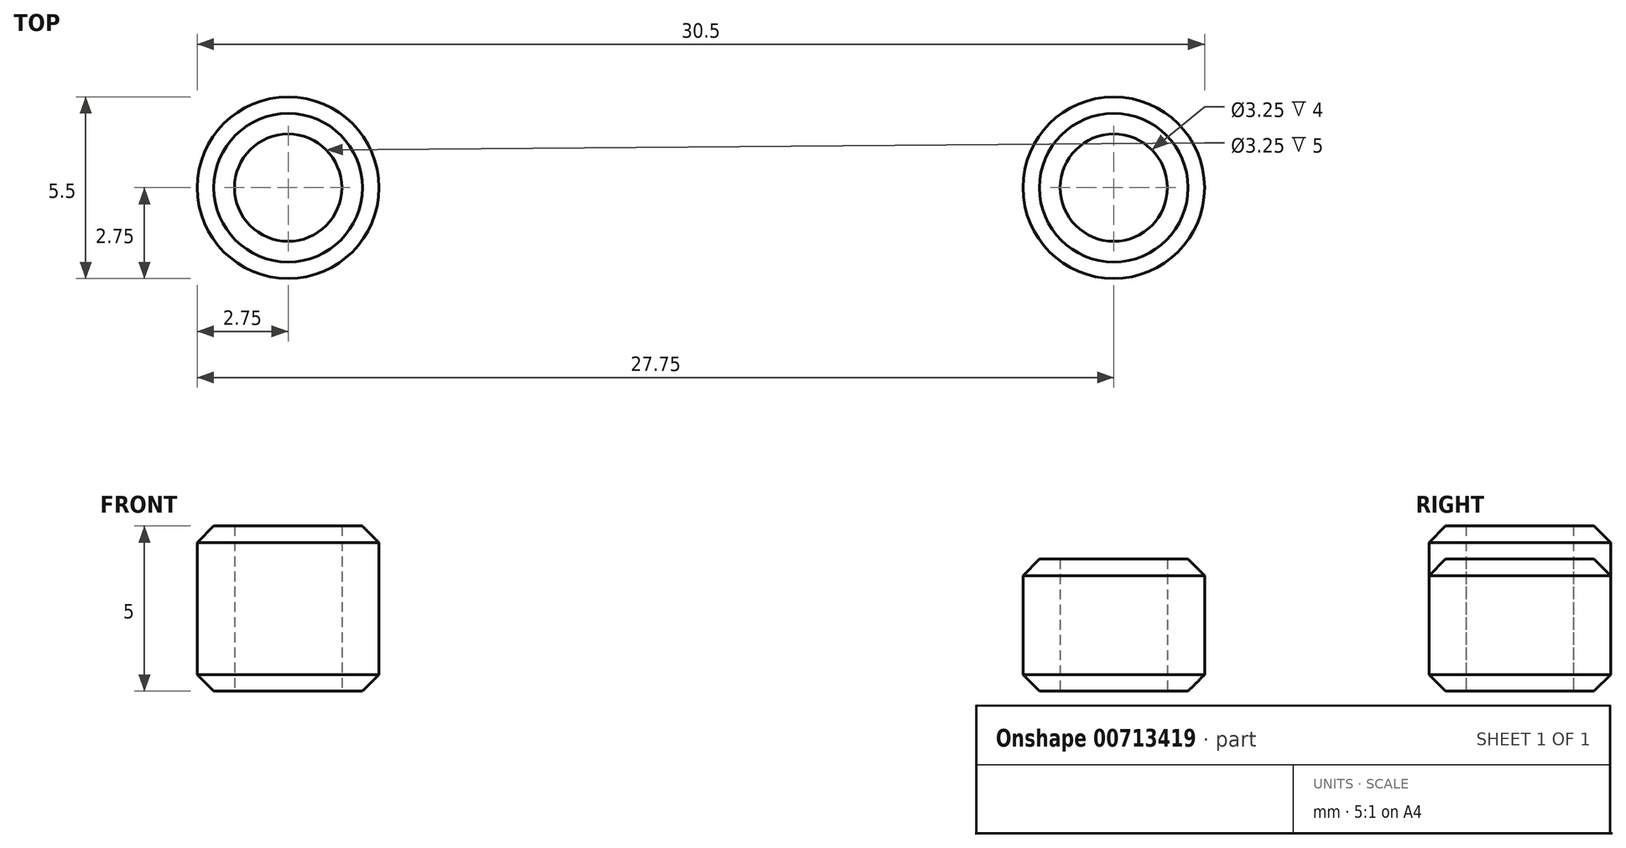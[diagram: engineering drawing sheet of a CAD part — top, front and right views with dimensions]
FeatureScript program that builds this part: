
annotation { "Feature Type Name" : "Feature", "Feature Type Description" : "" }
export const myFeature = defineFeature(function(context is Context, id is Id, definition is map)
    precondition{}
    {
        {
            var Q0;
            Q0=qCreatedBy(makeId("Top.planeOp"),FACE);
            var sketch = newSketch(context, id + "F0", { "sketchPlane" : qUnion([Q0])});
            skCircle(sketch, "E0", {"center": v(0, 0) * mm, "radius": 2.75 * mm});
            skCircle(sketch, "E1", {"center": v(0, 0) * mm, "radius": 1.63 * mm});
            skCircle(sketch, "E2.1.0.0", {"center": v(25, 0) * mm, "radius": 1.63 * mm});
            skCircle(sketch, "E2.1.0.1", {"center": v(25, 0) * mm, "radius": 2.75 * mm});
            skLineSegment(sketch, "E2.direction1", {"start": v(0, 0) * mm, "end": v(25, 0) * mm, "construction": true});
            skSolve(sketch);
        }
        {
            var Q0;
            Q0=makeQuery(id+"F0.imprint","IMPRINT",FACE,{"disambiguationData":[TD([[makeQuery(id+"F0.imprint","IMPRINT",EDGE,{"derivedFrom":sQuery(id+"F0.wireOp",EDGE,"E0")}),1.0]])]});
            extrude(context, id + "F1", {"entities" : qUnion([Q0]), "depth" : 5 * mm, "offsetDistance" : 25 * mm});
        }
        {
            var Q0;
            Q0=makeQuery(id+"F0.imprint","IMPRINT",FACE,{"disambiguationData":[TD([[makeQuery(id+"F0.imprint","IMPRINT",EDGE,{"derivedFrom":sQuery(id+"F0.wireOp",EDGE,"E2.1.0.0")}),-1.0]])]});
            extrude(context, id + "F2", {"entities" : qUnion([Q0]), "depth" : 4 * mm, "offsetDistance" : 25 * mm});
        }
        {
            var Q0;
            Q0=makeQuery(id+"F1.opExtrude","CAP_EDGE",EDGE,{"disambiguationData":[OSD([sQuery(id+"F0.wireOp",EDGE,"E0")])],"isStart":false});
            var Q1;
            Q1=makeQuery(id+"F1.opExtrude","CAP_EDGE",EDGE,{"disambiguationData":[OSD([sQuery(id+"F0.wireOp",EDGE,"E0")])],"isStart":true});
            var Q2;
            Q2=makeQuery(id+"F2.opExtrude","CAP_EDGE",EDGE,{"disambiguationData":[OSD([sQuery(id+"F0.wireOp",EDGE,"E2.1.0.1")])],"isStart":true});
            var Q3;
            Q3=makeQuery(id+"F2.opExtrude","CAP_EDGE",EDGE,{"disambiguationData":[OSD([sQuery(id+"F0.wireOp",EDGE,"E2.1.0.1")])],"isStart":false});
            chamfer(context, id + "F3", {"entities" : qUnion([Q0, Q1, Q2, Q3]), "width" : 0.5 * mm, "tangentPropagation" : true});
        }
    });
